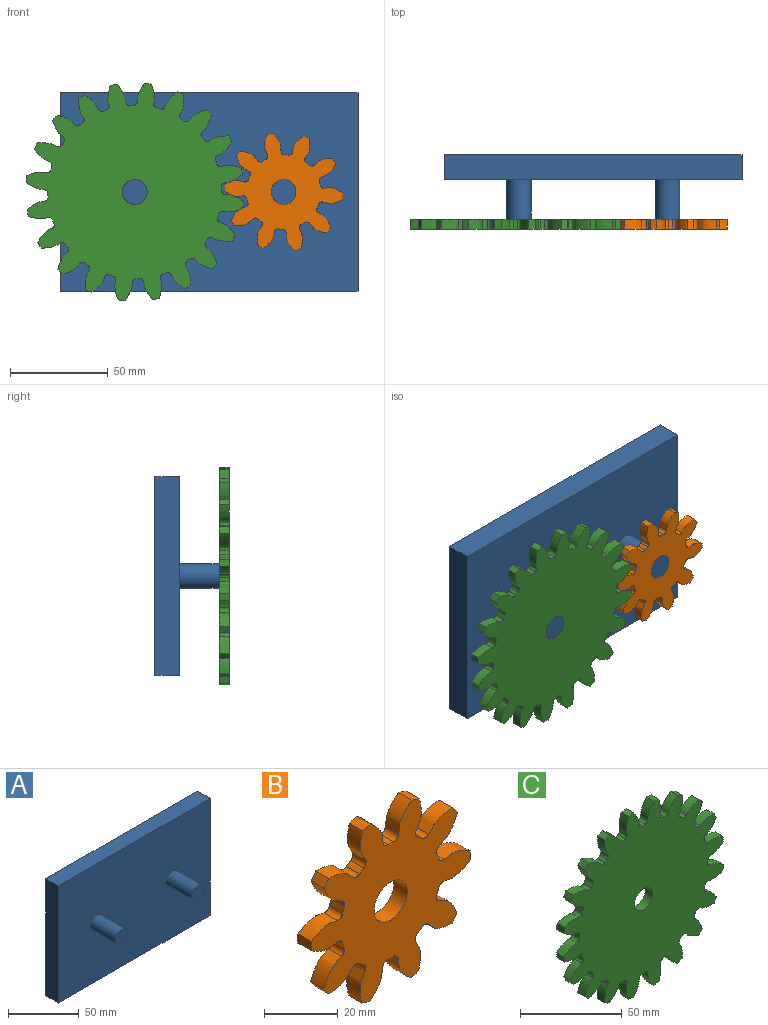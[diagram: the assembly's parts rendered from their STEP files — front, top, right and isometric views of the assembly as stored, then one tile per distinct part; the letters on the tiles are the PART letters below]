
ASSEMBLY  parts=3 mates=2
PART A: 10 faces, bbox 152.4x38.1x101.6 mm
  f0: plane 101.6x12.7mm, normal (-1,0,0), area 1290.3mm2, adj f1,f3,f4,f5
  f1: plane 152.4x12.7mm, normal (0,0,-1), area 1935.5mm2, adj f0,f2,f4,f5
  f2: plane 101.6x12.7mm, normal (1,0,0), area 1290.3mm2, adj f1,f3,f4,f5
  f3: plane 152.4x12.7mm, normal (0,0,1), area 1935.5mm2, adj f0,f2,f4,f5
  f4: plane 152.4x101.6mm, normal (0,-1,0), area 15230.5mm2, adj f0,f1,f2,f3,f6,f8
  f5: plane 152.4x101.6mm, normal (0,1,0), area 15483.8mm2, adj f0,f1,f2,f3
  f6: cylinder r=6.35mm len=25.4mm, axis (0,1,0), area 1013.4mm2, adj f4,f7
  f7: plane 12.7x12.7mm, normal (0,-1,0), area 126.7mm2, adj f6
  f8: cylinder r=6.35mm len=25.4mm, axis (0,1,0), area 1013.4mm2, adj f4,f9
  f9: plane 12.7x12.7mm, normal (0,-1,0), area 126.7mm2, adj f8
PART B: 63 faces, bbox 61.1x5.1x59 mm
  f0: extruded ~9.96x5.08mm, area 53.5mm2, adj f40,f41,f42,f43
  f1: cylinder r=19.05mm len=5.08mm, axis (0,1,0), area 10.8mm2, adj f41,f42,f43,f44
  f2: extruded ~7.5x6.89mm, area 53.5mm2, adj f3,f41,f42,f44
  f3: cylinder r=30.48mm len=5.08mm, axis (0,1,0), area 15.2mm2, adj f2,f4,f41,f42
  f4: extruded ~9.31x5.08mm, area 53.5mm2, adj f3,f41,f42,f45
  f5: cylinder r=19.05mm len=5.08mm, axis (0,1,0), area 10.8mm2, adj f41,f42,f45,f46
  f6: extruded ~10.12x5.08mm, area 53.5mm2, adj f7,f41,f42,f46
  f7: cylinder r=30.48mm len=5.08mm, axis (0,1,0), area 15.2mm2, adj f6,f8,f41,f42
  f8: extruded ~8.82x5.1mm, area 53.5mm2, adj f7,f41,f42,f47
  f9: cylinder r=19.05mm len=5.08mm, axis (0,1,0), area 10.8mm2, adj f41,f42,f47,f48
  f10: extruded ~8.87x5.08mm, area 53.5mm2, adj f11,f41,f42,f48
  f11: cylinder r=30.48mm len=5.08mm, axis (0,1,0), area 15.2mm2, adj f10,f12,f41,f42
  f12: extruded ~10.13x5.08mm, area 53.5mm2, adj f11,f41,f42,f49
  f13: cylinder r=19.05mm len=5.08mm, axis (0,1,0), area 10.8mm2, adj f41,f42,f49,f50
  f14: extruded ~9.26x5.08mm, area 53.5mm2, adj f15,f41,f42,f50
  f15: cylinder r=30.48mm len=5.08mm, axis (0,1,0), area 15.2mm2, adj f14,f16,f41,f42
  f16: extruded ~7.57x6.82mm, area 53.5mm2, adj f15,f41,f42,f51
  f17: cylinder r=19.05mm len=5.08mm, axis (0,1,0), area 10.8mm2, adj f41,f42,f51,f52
  f18: extruded ~9.99x5.08mm, area 53.5mm2, adj f19,f41,f42,f52
  f19: cylinder r=30.48mm len=5.08mm, axis (0,1,0), area 15.2mm2, adj f18,f20,f41,f42
  f20: extruded ~9.96x5.08mm, area 53.5mm2, adj f19,f41,f42,f53
  f21: cylinder r=19.05mm len=5.08mm, axis (0,1,0), area 10.8mm2, adj f41,f42,f53,f54
  f22: extruded ~7.5x6.89mm, area 53.5mm2, adj f23,f41,f42,f54
  f23: cylinder r=30.48mm len=5.08mm, axis (0,1,0), area 15.2mm2, adj f22,f24,f41,f42
  f24: extruded ~9.31x5.08mm, area 53.5mm2, adj f23,f41,f42,f55
  f25: cylinder r=19.05mm len=5.08mm, axis (0,1,0), area 10.8mm2, adj f41,f42,f55,f56
  f26: extruded ~10.12x5.08mm, area 53.5mm2, adj f27,f41,f42,f56
  f27: cylinder r=30.48mm len=5.08mm, axis (0,1,0), area 15.2mm2, adj f26,f28,f41,f42
  f28: extruded ~8.82x5.1mm, area 53.5mm2, adj f27,f41,f42,f57
  f29: cylinder r=19.05mm len=5.08mm, axis (0,1,0), area 10.8mm2, adj f41,f42,f57,f58
  f30: extruded ~8.87x5.08mm, area 53.5mm2, adj f31,f41,f42,f58
  f31: cylinder r=30.48mm len=5.08mm, axis (0,1,0), area 15.2mm2, adj f30,f32,f41,f42
  f32: extruded ~10.13x5.08mm, area 53.5mm2, adj f31,f41,f42,f59
  f33: cylinder r=19.05mm len=5.08mm, axis (0,1,0), area 10.8mm2, adj f41,f42,f59,f60
  f34: extruded ~9.26x5.08mm, area 53.5mm2, adj f35,f41,f42,f60
  f35: cylinder r=30.48mm len=5.08mm, axis (0,1,0), area 15.2mm2, adj f34,f36,f41,f42
  f36: extruded ~7.57x6.82mm, area 53.5mm2, adj f35,f41,f42,f61
  f37: cylinder r=19.05mm len=5.08mm, axis (0,1,0), area 10.8mm2, adj f41,f42,f61,f62
  f38: extruded ~9.99x5.08mm, area 53.5mm2, adj f40,f41,f42,f62
  f39: cylinder r=6.35mm len=12.7mm, axis (0,1,0), area 202.7mm2, adj f41,f42
  f40: cylinder r=30.48mm len=5.08mm, axis (0,1,0), area 15.2mm2, adj f0,f38,f41,f42
  f41: plane 61.08x59.04mm, normal (0,-1,0), area 1808.1mm2, adj f0,f1,f2,f3,f4,f5,f6,f7
  f42: plane 61.08x59.04mm, normal (0,1,0), area 1808.1mm2, adj f0,f1,f2,f3,f4,f5,f6,f7
  f43: cylinder r=1.8mm len=5.08mm, axis (0,1,0), area 13.6mm2, adj f0,f1,f41,f42
  f44: cylinder r=1.8mm len=5.08mm, axis (0,1,0), area 13.6mm2, adj f1,f2,f41,f42
  f45: cylinder r=1.8mm len=5.08mm, axis (0,1,0), area 13.6mm2, adj f4,f5,f41,f42
  f46: cylinder r=1.8mm len=5.08mm, axis (0,1,0), area 13.6mm2, adj f5,f6,f41,f42
  f47: cylinder r=1.8mm len=5.08mm, axis (0,1,0), area 13.6mm2, adj f8,f9,f41,f42
  f48: cylinder r=1.8mm len=5.08mm, axis (0,1,0), area 13.6mm2, adj f9,f10,f41,f42
  f49: cylinder r=1.8mm len=5.08mm, axis (0,1,0), area 13.6mm2, adj f12,f13,f41,f42
  f50: cylinder r=1.8mm len=5.08mm, axis (0,1,0), area 13.6mm2, adj f13,f14,f41,f42
  f51: cylinder r=1.8mm len=5.08mm, axis (0,1,0), area 13.6mm2, adj f16,f17,f41,f42
  f52: cylinder r=1.8mm len=5.08mm, axis (0,1,0), area 13.6mm2, adj f17,f18,f41,f42
  f53: cylinder r=1.8mm len=5.08mm, axis (0,1,0), area 13.6mm2, adj f20,f21,f41,f42
  f54: cylinder r=1.8mm len=5.08mm, axis (0,1,0), area 13.6mm2, adj f21,f22,f41,f42
  f55: cylinder r=1.8mm len=5.08mm, axis (0,1,0), area 13.6mm2, adj f24,f25,f41,f42
  f56: cylinder r=1.8mm len=5.08mm, axis (0,1,0), area 13.6mm2, adj f25,f26,f41,f42
  f57: cylinder r=1.8mm len=5.08mm, axis (0,1,0), area 13.6mm2, adj f28,f29,f41,f42
  f58: cylinder r=1.8mm len=5.08mm, axis (0,1,0), area 13.6mm2, adj f29,f30,f41,f42
  f59: cylinder r=1.8mm len=5.08mm, axis (0,1,0), area 13.6mm2, adj f32,f33,f41,f42
  f60: cylinder r=1.8mm len=5.08mm, axis (0,1,0), area 13.6mm2, adj f33,f34,f41,f42
  f61: cylinder r=1.8mm len=5.08mm, axis (0,1,0), area 13.6mm2, adj f36,f37,f41,f42
  f62: cylinder r=1.8mm len=5.08mm, axis (0,1,0), area 13.6mm2, adj f37,f38,f41,f42
PART C: 123 faces, bbox 111x5.1x111 mm
  f0: extruded ~9.23x5.08mm, area 52.3mm2, adj f80,f81,f82,f83
  f1: cylinder r=44.45mm len=5.08mm, axis (0,1,0), area 10.3mm2, adj f81,f82,f83,f84
  f2: extruded ~9.23x5.08mm, area 52.3mm2, adj f3,f81,f82,f84
  f3: cylinder r=55.88mm len=5.08mm, axis (0,1,0), area 17.9mm2, adj f2,f4,f81,f82
  f4: extruded ~10.04x5.08mm, area 52.3mm2, adj f3,f81,f82,f85
  f5: cylinder r=44.45mm len=5.08mm, axis (0,1,0), area 10.3mm2, adj f81,f82,f85,f86
  f6: extruded ~7.53x6.71mm, area 52.3mm2, adj f7,f81,f82,f86
  f7: cylinder r=55.88mm len=5.08mm, axis (0,1,0), area 17.9mm2, adj f6,f8,f81,f82
  f8: extruded ~9.86x5.08mm, area 52.3mm2, adj f7,f81,f82,f87
  f9: cylinder r=44.45mm len=5.08mm, axis (0,1,0), area 10.3mm2, adj f81,f82,f87,f88
  f10: extruded ~8.71x5.09mm, area 52.3mm2, adj f11,f81,f82,f88
  f11: cylinder r=55.88mm len=5.08mm, axis (0,1,0), area 17.9mm2, adj f10,f12,f81,f82
  f12: extruded ~8.71x5.09mm, area 52.3mm2, adj f11,f81,f82,f89
  f13: cylinder r=44.45mm len=5.08mm, axis (0,1,0), area 10.3mm2, adj f81,f82,f89,f90
  f14: extruded ~9.86x5.08mm, area 52.3mm2, adj f15,f81,f82,f90
  f15: cylinder r=55.88mm len=5.08mm, axis (0,1,0), area 17.9mm2, adj f14,f16,f81,f82
  f16: extruded ~7.53x6.71mm, area 52.3mm2, adj f15,f81,f82,f91
  f17: cylinder r=44.45mm len=5.08mm, axis (0,1,0), area 10.3mm2, adj f81,f82,f91,f92
  f18: extruded ~10.04x5.08mm, area 52.3mm2, adj f19,f81,f82,f92
  f19: cylinder r=55.88mm len=5.08mm, axis (0,1,0), area 17.9mm2, adj f18,f20,f81,f82
  f20: extruded ~9.23x5.08mm, area 52.3mm2, adj f19,f81,f82,f93
  f21: cylinder r=44.45mm len=5.08mm, axis (0,1,0), area 10.3mm2, adj f81,f82,f93,f94
  f22: extruded ~9.23x5.08mm, area 52.3mm2, adj f23,f81,f82,f94
  f23: cylinder r=55.88mm len=5.08mm, axis (0,1,0), area 17.9mm2, adj f22,f24,f81,f82
  f24: extruded ~10.04x5.08mm, area 52.3mm2, adj f23,f81,f82,f95
  f25: cylinder r=44.45mm len=5.08mm, axis (0,1,0), area 10.3mm2, adj f81,f82,f95,f96
  f26: extruded ~7.53x6.71mm, area 52.3mm2, adj f27,f81,f82,f96
  f27: cylinder r=55.88mm len=5.08mm, axis (0,1,0), area 17.9mm2, adj f26,f28,f81,f82
  f28: extruded ~9.86x5.08mm, area 52.3mm2, adj f27,f81,f82,f97
  f29: cylinder r=44.45mm len=5.08mm, axis (0,1,0), area 10.3mm2, adj f81,f82,f97,f98
  f30: extruded ~8.71x5.09mm, area 52.3mm2, adj f31,f81,f82,f98
  f31: cylinder r=55.88mm len=5.08mm, axis (0,1,0), area 17.9mm2, adj f30,f32,f81,f82
  f32: extruded ~8.71x5.09mm, area 52.3mm2, adj f31,f81,f82,f99
  f33: cylinder r=44.45mm len=5.08mm, axis (0,1,0), area 10.3mm2, adj f81,f82,f99,f100
  f34: extruded ~9.86x5.08mm, area 52.3mm2, adj f35,f81,f82,f100
  f35: cylinder r=55.88mm len=5.08mm, axis (0,1,0), area 17.9mm2, adj f34,f36,f81,f82
  f36: extruded ~7.53x6.71mm, area 52.3mm2, adj f35,f81,f82,f101
  f37: cylinder r=44.45mm len=5.08mm, axis (0,1,0), area 10.3mm2, adj f81,f82,f101,f102
  f38: extruded ~10.04x5.08mm, area 52.3mm2, adj f39,f81,f82,f102
  f39: cylinder r=55.88mm len=5.08mm, axis (0,1,0), area 17.9mm2, adj f38,f40,f81,f82
  f40: extruded ~9.23x5.08mm, area 52.3mm2, adj f39,f81,f82,f103
  f41: cylinder r=44.45mm len=5.08mm, axis (0,1,0), area 10.3mm2, adj f81,f82,f103,f104
  f42: extruded ~9.23x5.08mm, area 52.3mm2, adj f43,f81,f82,f104
  f43: cylinder r=55.88mm len=5.08mm, axis (0,1,0), area 17.9mm2, adj f42,f44,f81,f82
  f44: extruded ~10.04x5.08mm, area 52.3mm2, adj f43,f81,f82,f105
  f45: cylinder r=44.45mm len=5.08mm, axis (0,1,0), area 10.3mm2, adj f81,f82,f105,f106
  f46: extruded ~7.53x6.71mm, area 52.3mm2, adj f47,f81,f82,f106
  f47: cylinder r=55.88mm len=5.08mm, axis (0,1,0), area 17.9mm2, adj f46,f48,f81,f82
  f48: extruded ~9.86x5.08mm, area 52.3mm2, adj f47,f81,f82,f107
  f49: cylinder r=44.45mm len=5.08mm, axis (0,1,0), area 10.3mm2, adj f81,f82,f107,f108
  f50: extruded ~8.71x5.09mm, area 52.3mm2, adj f51,f81,f82,f108
  f51: cylinder r=55.88mm len=5.08mm, axis (0,1,0), area 17.9mm2, adj f50,f52,f81,f82
  f52: extruded ~8.71x5.09mm, area 52.3mm2, adj f51,f81,f82,f109
  f53: cylinder r=44.45mm len=5.08mm, axis (0,1,0), area 10.3mm2, adj f81,f82,f109,f110
  f54: extruded ~9.86x5.08mm, area 52.3mm2, adj f55,f81,f82,f110
  f55: cylinder r=55.88mm len=5.08mm, axis (0,1,0), area 17.9mm2, adj f54,f56,f81,f82
  f56: extruded ~7.53x6.71mm, area 52.3mm2, adj f55,f81,f82,f111
  f57: cylinder r=44.45mm len=5.08mm, axis (0,1,0), area 10.3mm2, adj f81,f82,f111,f112
  f58: extruded ~10.04x5.08mm, area 52.3mm2, adj f59,f81,f82,f112
  f59: cylinder r=55.88mm len=5.08mm, axis (0,1,0), area 17.9mm2, adj f58,f60,f81,f82
  f60: extruded ~9.23x5.08mm, area 52.3mm2, adj f59,f81,f82,f113
  f61: cylinder r=44.45mm len=5.08mm, axis (0,1,0), area 10.3mm2, adj f81,f82,f113,f114
  f62: extruded ~9.23x5.08mm, area 52.3mm2, adj f63,f81,f82,f114
  f63: cylinder r=55.88mm len=5.08mm, axis (0,1,0), area 17.9mm2, adj f62,f64,f81,f82
  f64: extruded ~10.04x5.08mm, area 52.3mm2, adj f63,f81,f82,f115
  f65: cylinder r=44.45mm len=5.08mm, axis (0,1,0), area 10.3mm2, adj f81,f82,f115,f116
  f66: extruded ~7.53x6.71mm, area 52.3mm2, adj f67,f81,f82,f116
  f67: cylinder r=55.88mm len=5.08mm, axis (0,1,0), area 17.9mm2, adj f66,f68,f81,f82
  f68: extruded ~9.86x5.08mm, area 52.3mm2, adj f67,f81,f82,f117
  f69: cylinder r=44.45mm len=5.08mm, axis (0,1,0), area 10.3mm2, adj f81,f82,f117,f118
  f70: extruded ~8.71x5.09mm, area 52.3mm2, adj f71,f81,f82,f118
  f71: cylinder r=55.88mm len=5.08mm, axis (0,1,0), area 17.9mm2, adj f70,f72,f81,f82
  f72: extruded ~8.71x5.09mm, area 52.3mm2, adj f71,f81,f82,f119
  f73: cylinder r=44.45mm len=5.08mm, axis (0,1,0), area 10.3mm2, adj f81,f82,f119,f120
  f74: extruded ~9.86x5.08mm, area 52.3mm2, adj f75,f81,f82,f120
  f75: cylinder r=55.88mm len=5.08mm, axis (0,1,0), area 17.9mm2, adj f74,f76,f81,f82
  f76: extruded ~7.53x6.71mm, area 52.3mm2, adj f75,f81,f82,f121
  f77: cylinder r=44.45mm len=5.08mm, axis (0,1,0), area 10.3mm2, adj f81,f82,f121,f122
  f78: extruded ~10.04x5.08mm, area 52.3mm2, adj f80,f81,f82,f122
  f79: cylinder r=6.35mm len=12.7mm, axis (0,1,0), area 202.7mm2, adj f81,f82
  f80: cylinder r=55.88mm len=5.08mm, axis (0,1,0), area 17.9mm2, adj f0,f78,f81,f82
  f81: plane 110.96x110.96mm, normal (0,-1,0), area 7813mm2, adj f0,f1,f2,f3,f4,f5,f6,f7
  f82: plane 110.96x110.96mm, normal (0,1,0), area 7813mm2, adj f0,f1,f2,f3,f4,f5,f6,f7
  f83: cylinder r=1.88mm len=5.08mm, axis (0,1,0), area 14.7mm2, adj f0,f1,f81,f82
  f84: cylinder r=1.88mm len=5.08mm, axis (0,1,0), area 14.7mm2, adj f1,f2,f81,f82
  f85: cylinder r=1.88mm len=5.08mm, axis (0,1,0), area 14.7mm2, adj f4,f5,f81,f82
  f86: cylinder r=1.88mm len=5.08mm, axis (0,1,0), area 14.7mm2, adj f5,f6,f81,f82
  f87: cylinder r=1.88mm len=5.08mm, axis (0,1,0), area 14.7mm2, adj f8,f9,f81,f82
  f88: cylinder r=1.88mm len=5.08mm, axis (0,1,0), area 14.7mm2, adj f9,f10,f81,f82
  f89: cylinder r=1.88mm len=5.08mm, axis (0,1,0), area 14.7mm2, adj f12,f13,f81,f82
  f90: cylinder r=1.88mm len=5.08mm, axis (0,1,0), area 14.7mm2, adj f13,f14,f81,f82
  f91: cylinder r=1.88mm len=5.08mm, axis (0,1,0), area 14.7mm2, adj f16,f17,f81,f82
  f92: cylinder r=1.88mm len=5.08mm, axis (0,1,0), area 14.7mm2, adj f17,f18,f81,f82
  f93: cylinder r=1.88mm len=5.08mm, axis (0,1,0), area 14.7mm2, adj f20,f21,f81,f82
  f94: cylinder r=1.88mm len=5.08mm, axis (0,1,0), area 14.7mm2, adj f21,f22,f81,f82
  f95: cylinder r=1.88mm len=5.08mm, axis (0,1,0), area 14.7mm2, adj f24,f25,f81,f82
  f96: cylinder r=1.88mm len=5.08mm, axis (0,1,0), area 14.7mm2, adj f25,f26,f81,f82
  f97: cylinder r=1.88mm len=5.08mm, axis (0,1,0), area 14.7mm2, adj f28,f29,f81,f82
  f98: cylinder r=1.88mm len=5.08mm, axis (0,1,0), area 14.7mm2, adj f29,f30,f81,f82
  f99: cylinder r=1.88mm len=5.08mm, axis (0,1,0), area 14.7mm2, adj f32,f33,f81,f82
  f100: cylinder r=1.88mm len=5.08mm, axis (0,1,0), area 14.7mm2, adj f33,f34,f81,f82
  f101: cylinder r=1.88mm len=5.08mm, axis (0,1,0), area 14.7mm2, adj f36,f37,f81,f82
  f102: cylinder r=1.88mm len=5.08mm, axis (0,1,0), area 14.7mm2, adj f37,f38,f81,f82
  f103: cylinder r=1.88mm len=5.08mm, axis (0,1,0), area 14.7mm2, adj f40,f41,f81,f82
  f104: cylinder r=1.88mm len=5.08mm, axis (0,1,0), area 14.7mm2, adj f41,f42,f81,f82
  f105: cylinder r=1.88mm len=5.08mm, axis (0,1,0), area 14.7mm2, adj f44,f45,f81,f82
  f106: cylinder r=1.88mm len=5.08mm, axis (0,1,0), area 14.7mm2, adj f45,f46,f81,f82
  f107: cylinder r=1.88mm len=5.08mm, axis (0,1,0), area 14.7mm2, adj f48,f49,f81,f82
  f108: cylinder r=1.88mm len=5.08mm, axis (0,1,0), area 14.7mm2, adj f49,f50,f81,f82
  f109: cylinder r=1.88mm len=5.08mm, axis (0,1,0), area 14.7mm2, adj f52,f53,f81,f82
  f110: cylinder r=1.88mm len=5.08mm, axis (0,1,0), area 14.7mm2, adj f53,f54,f81,f82
  f111: cylinder r=1.88mm len=5.08mm, axis (0,1,0), area 14.7mm2, adj f56,f57,f81,f82
  f112: cylinder r=1.88mm len=5.08mm, axis (0,1,0), area 14.7mm2, adj f57,f58,f81,f82
  f113: cylinder r=1.88mm len=5.08mm, axis (0,1,0), area 14.7mm2, adj f60,f61,f81,f82
  f114: cylinder r=1.88mm len=5.08mm, axis (0,1,0), area 14.7mm2, adj f61,f62,f81,f82
  f115: cylinder r=1.88mm len=5.08mm, axis (0,1,0), area 14.7mm2, adj f64,f65,f81,f82
  f116: cylinder r=1.88mm len=5.08mm, axis (0,1,0), area 14.7mm2, adj f65,f66,f81,f82
  f117: cylinder r=1.88mm len=5.08mm, axis (0,1,0), area 14.7mm2, adj f68,f69,f81,f82
  f118: cylinder r=1.88mm len=5.08mm, axis (0,1,0), area 14.7mm2, adj f69,f70,f81,f82
  f119: cylinder r=1.88mm len=5.08mm, axis (0,1,0), area 14.7mm2, adj f72,f73,f81,f82
  f120: cylinder r=1.88mm len=5.08mm, axis (0,1,0), area 14.7mm2, adj f73,f74,f81,f82
  f121: cylinder r=1.88mm len=5.08mm, axis (0,1,0), area 14.7mm2, adj f76,f77,f81,f82
  f122: cylinder r=1.88mm len=5.08mm, axis (0,1,0), area 14.7mm2, adj f77,f78,f81,f82
PLACE A t=(-34.68,-5.18,-6.3)mm fixed
PLACE B rot(axis=(0,1,0),112.2deg) t=(3.42,-38.2,-6.3)mm
PLACE C rot(axis=(0,1,0),123.9deg) t=(-72.78,-38.2,-6.3)mm
MATE revolute C.f3 <-> A.f6  axis (0,-1,0) through (-72.78,-43.28,-6.3)mm
MATE revolute B.f3 <-> A.f8  axis (0,-1,0) through (3.42,-43.28,-6.3)mm
